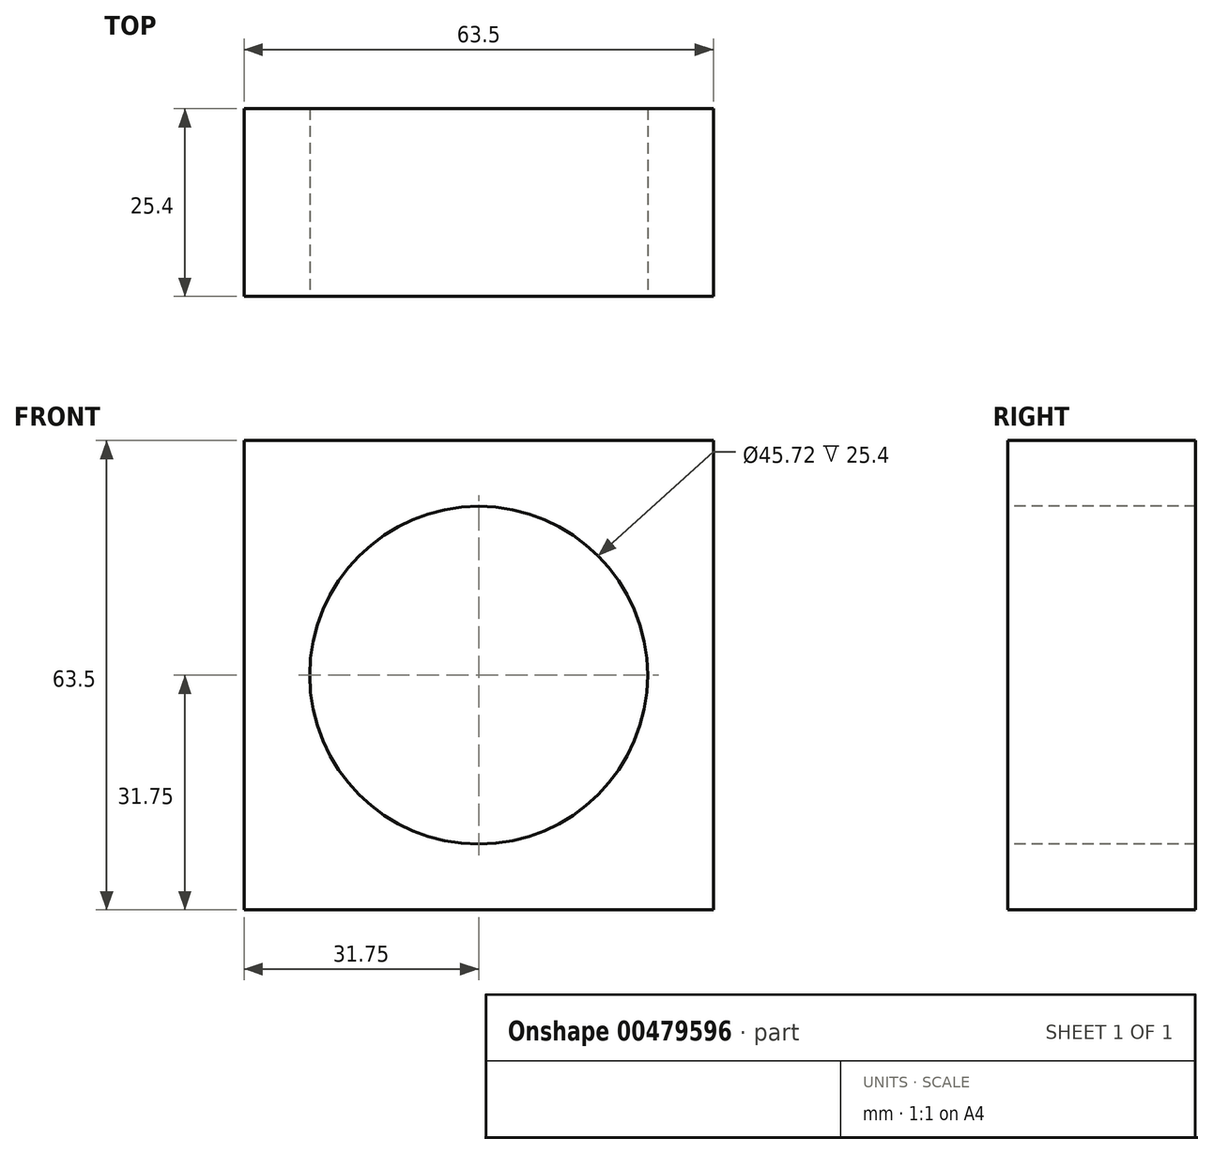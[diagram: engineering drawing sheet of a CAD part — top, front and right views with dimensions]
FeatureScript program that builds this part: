
annotation { "Feature Type Name" : "Feature", "Feature Type Description" : "" }
export const myFeature = defineFeature(function(context is Context, id is Id, definition is map)
    precondition{}
    {
        {
            var Q0;
            Q0=qCreatedBy(makeId("Front.planeOp"),FACE);
            var sketch = newSketch(context, id + "F0", { "sketchPlane" : qUnion([Q0])});
            skPoint(sketch, "E0.middle", {"position": v(0, 0) * mm});
            skCircle(sketch, "E1", {"center": v(0, 0) * mm, "radius": 22.86 * mm});
            skLineSegment(sketch, "E2.bottom", {"start": v(31.75, -31.75) * mm, "end": v(-31.75, -31.75) * mm});
            skLineSegment(sketch, "E2.top", {"start": v(31.75, 31.75) * mm, "end": v(-31.75, 31.75) * mm});
            skLineSegment(sketch, "E2.left", {"start": v(31.75, -31.75) * mm, "end": v(31.75, 31.75) * mm});
            skLineSegment(sketch, "E2.right", {"start": v(-31.75, -31.75) * mm, "end": v(-31.75, 31.75) * mm});
            skSolve(sketch);
        }
        {
            var Q0;
            Q0=makeQuery(id+"F0.imprint","IMPRINT",FACE,{"disambiguationData":[TD([[makeQuery(id+"F0.imprint","IMPRINT",EDGE,{"derivedFrom":sQuery(id+"F0.wireOp",EDGE,"E1")}),-1.0]])]});
            extrude(context, id + "F1", {"entities" : qUnion([Q0]), "oppositeDirection" : true, "depth" : 25.4 * mm});
        }
    });
